# Revit family: NLRS_30_GM_FB_073150_GB
name_source: partatom
category: Generic Models
units: mm (PartAtom-declared; Revit-internal decimal feet)

## family parameters
Can host rebar = No
Cut with Voids When Loaded = No
Host = Face
Part Type = Normal
Room Calculation Point = No
Round Connector Dimension = Use Diameter
Shared = Yes

## types (1)
- XL-Hoekanker 75x150 SV
    B = 72 mm  [stored 0.23622 ft]
    Change_placement = No
    D = 5 mm  [stored 0.0164042 ft]
    Default Elevation = 1219 mm
    Description = XL-Hoekanker 75x150
    GB_ID_Gatenpatroon = 10/7-8/9-2/13
    GB_ID_Slobgaten = 2/30x13
    GB_ID_Verpakkingseenheid = 30
    GB_X2_Anchor 2 = 0 mm  [stored 0 ft]
    GB_X2_Anchor 4 = 0 mm  [stored 0 ft]
    GB_X_Anchor 2 = 0 mm  [stored 0 ft]
    GB_X_Anchor 4 = 0 mm  [stored 0 ft]
    GB_X_Screw 1 = 18 mm
    GB_X_Screw 2 = 18 mm
    GB_X_Screw 3 = 18 mm
    GB_X_Screw 4 = 25 mm  [stored 0.082021 ft]
    GB_Y_Anchor 1 = 38 mm
    GB_Y_Anchor 2 = 0 mm  [stored 0 ft]
    GB_Y_Anchor 3 = 126 mm
    GB_Y_Anchor 4 = 36 mm
    GB_Y_Screw 1 = 40 mm  [stored 0.131234 ft]
    GB_Y_Screw 2 = 60 mm  [stored 0.19685 ft]
    GB_Y_Screw 3 = 106 mm
    GB_Y_Screw 4 = 137 mm  [stored 0.449475 ft]
    I_01 Product Number = 73150
    I_03 Product Name = XL-Hoekanker 75x150
    IfcDescription = XL-Hoekanker 75x150
    IfcExportAs = MechanicalFastnerType
    IfcExportType = USERDEFINED
    L = 75 mm
    L1 = 150 mm
    Manufacturer = Gebr. Bodegraven B.V.
    Model = 75x100
    NLRS_C_bestemming = Element- en kozijnverbindingen
    NLRS_C_content_provider = Gebr. Bodegraven B.V.
    NLRS_C_content_versie = 1.0
    NLRS_C_fabrikant_product_code = 073150
    NLRS_C_gtin_code = 8714318036409
    NLRS_C_materiaal_afwerking = Sendzimir Verzinkt
    NLRS_C_omschrijving = XL-Hoekanker 75x150
    Type Image = 073150.jpg
    URL = https://www.gb.nl
    X2A2 = 0 mm  [stored 0 ft]
    X2A4 = 0 mm  [stored 0 ft]
    XA2 = 0 mm  [stored 0 ft]
    XA4 = 0 mm  [stored 0 ft]
    XS1 = 18 mm
    XS2 = 18 mm
    XS3 = 18 mm
    XS4 = 25 mm  [stored 0.082021 ft]
    YA1 = 38 mm
    YA2 = 0 mm  [stored 0 ft]
    YA3 = 126 mm
    YA4 = 36 mm
    YS1 = 40 mm  [stored 0.131234 ft]
    YS2 = 60 mm  [stored 0.19685 ft]
    YS3 = 106 mm
    YS4 = 137 mm  [stored 0.449475 ft]

note: [stored X ft] marks values corroborated as IEEE doubles in the binary element streams (Revit-internal decimal feet)

## geometry (parser evidence)
native form markers: Sweep x2
no freeform markers — native parametric forms only
